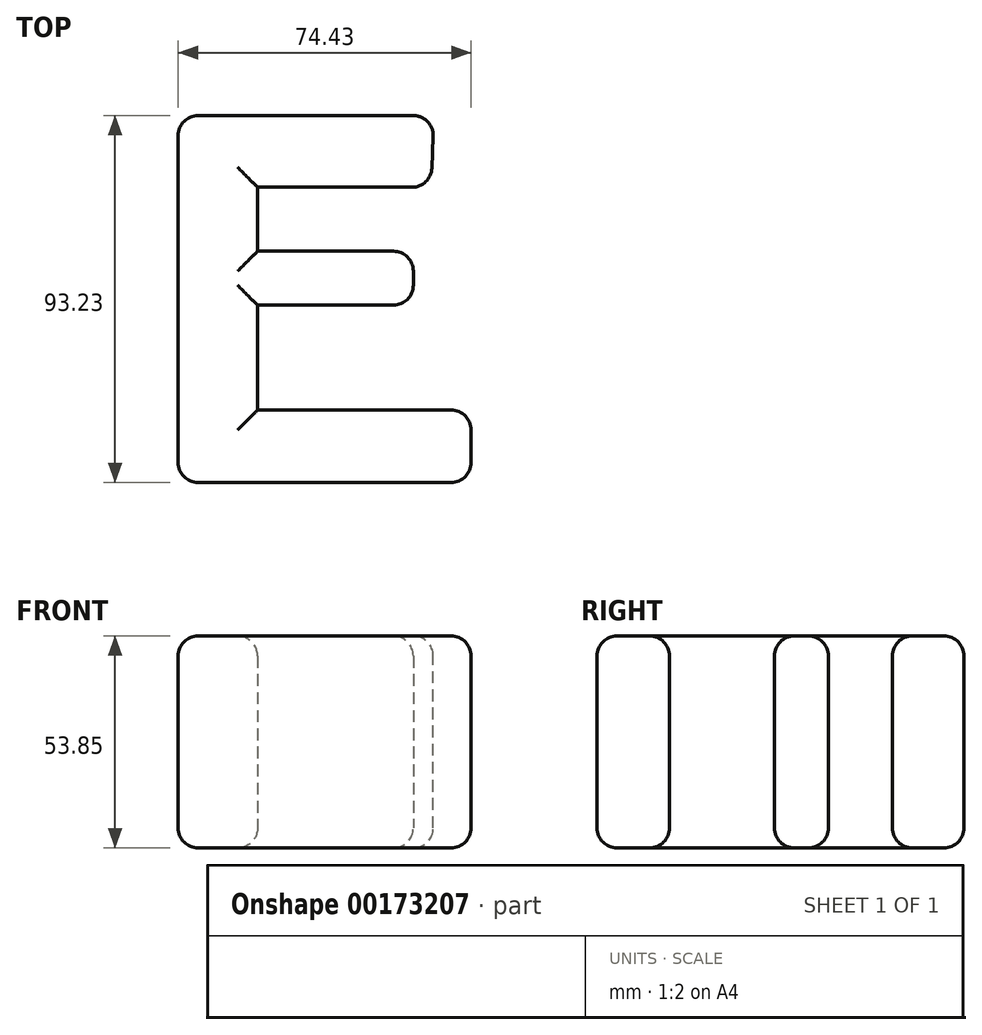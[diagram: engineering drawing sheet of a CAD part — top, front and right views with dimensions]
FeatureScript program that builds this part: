
annotation { "Feature Type Name" : "Feature", "Feature Type Description" : "" }
export const myFeature = defineFeature(function(context is Context, id is Id, definition is map)
    precondition{}
    {
        {
            var Q0;
            Q0=qCreatedBy(makeId("Top.planeOp"),FACE);
            var sketch = newSketch(context, id + "F0", { "sketchPlane" : qUnion([Q0])});
            skLineSegment(sketch, "E0", {"start": v(28, 52) * mm, "end": v(-37.02, 52) * mm});
            skLineSegment(sketch, "E1", {"start": v(-37.02, 52) * mm, "end": v(-37.02, -41.23) * mm});
            skLineSegment(sketch, "E2", {"start": v(-37.02, -41.23) * mm, "end": v(37.4, -41.23) * mm});
            skLineSegment(sketch, "E3", {"start": v(37.4, -41.23) * mm, "end": v(37.4, -22.82) * mm});
            skLineSegment(sketch, "E4", {"start": v(37.4, -22.82) * mm, "end": v(-16.84, -22.82) * mm});
            skLineSegment(sketch, "E5", {"start": v(-16.84, -22.82) * mm, "end": v(-16.84, -6.56) * mm});
            skLineSegment(sketch, "E6", {"start": v(-16.84, -6.56) * mm, "end": v(-16.84, 3.82) * mm});
            skLineSegment(sketch, "E7", {"start": v(-16.84, 3.82) * mm, "end": v(22.72, 3.82) * mm});
            skLineSegment(sketch, "E8", {"start": v(22.72, 3.82) * mm, "end": v(22.72, 17.53) * mm});
            skLineSegment(sketch, "E9", {"start": v(22.72, 17.53) * mm, "end": v(-16.84, 17.53) * mm});
            skLineSegment(sketch, "E10", {"start": v(-16.84, 17.53) * mm, "end": v(-16.84, 33.79) * mm});
            skLineSegment(sketch, "E11", {"start": v(-16.84, 33.79) * mm, "end": v(27.22, 33.79) * mm});
            skLineSegment(sketch, "E12", {"start": v(28, 52) * mm, "end": v(27.22, 33.79) * mm});
            skSolve(sketch);
        }
        {
            var Q0;
            Q0=makeQuery(id+"F0.imprint","IMPRINT",FACE,{"disambiguationData":[TD([[makeQuery(id+"F0.imprint","IMPRINT",EDGE,{"derivedFrom":sQuery(id+"F0.wireOp",EDGE,"E0")}),1.0]])]});
            extrude(context, id + "F1", {"entities" : qUnion([Q0]), "depth" : 53.85 * mm});
        }
        {
            var Q0;
            Q0=makeQuery(id+"F1.opExtrude","SWEPT_FACE",FACE,{"disambiguationData":[OSD([sQuery(id+"F0.wireOp",EDGE,"E12")])]});
            var Q1;
            Q1=makeQuery(id+"F1.opExtrude","SWEPT_FACE",FACE,{"disambiguationData":[OSD([sQuery(id+"F0.wireOp",EDGE,"E8")])]});
            var Q2;
            Q2=makeQuery(id+"F1.opExtrude","SWEPT_FACE",FACE,{"disambiguationData":[OSD([sQuery(id+"F0.wireOp",EDGE,"E3")])]});
            fillet(context, id + "F2", {"entities" : qUnion([Q0, Q1, Q2]), "radius" : 5.08 * mm, "tangentPropagation" : true, "allowEdgeOverflow" : false});
        }
        {
            var Q0;
            Q0=makeQuery(id+"F1.opExtrude","CAP_EDGE",EDGE,{"disambiguationData":[OSD([sQuery(id+"F0.wireOp",EDGE,"E2")])],"isStart":false});
            var Q1;
            Q1=makeQuery(id+"F1.opExtrude","CAP_EDGE",EDGE,{"disambiguationData":[OSD([sQuery(id+"F0.wireOp",EDGE,"E1")])],"isStart":false});
            var Q2;
            Q2=makeQuery(id+"F1.opExtrude","CAP_EDGE",EDGE,{"disambiguationData":[OSD([sQuery(id+"F0.wireOp",EDGE,"E0")])],"isStart":false});
            var Q3;
            Q3=makeQuery(id+"F1.opExtrude","CAP_EDGE",EDGE,{"disambiguationData":[OSD([sQuery(id+"F0.wireOp",EDGE,"E10")])],"isStart":false});
            var Q4;
            Q4=makeQuery(id+"F1.opExtrude","CAP_EDGE",EDGE,{"disambiguationData":[OSD([sQuery(id+"F0.wireOp",EDGE,"E11")])],"isStart":false});
            var Q5;
            Q5=makeQuery(id+"F1.opExtrude","CAP_EDGE",EDGE,{"disambiguationData":[OSD([sQuery(id+"F0.wireOp",EDGE,"E9")])],"isStart":false});
            var Q6;
            Q6=makeQuery(id+"F1.opExtrude","CAP_EDGE",EDGE,{"disambiguationData":[OSD([sQuery(id+"F0.wireOp",EDGE,"E7")])],"isStart":false});
            var Q7;
            Q7=makeQuery(id+"F1.opExtrude","CAP_EDGE",EDGE,{"disambiguationData":[OSD([sQuery(id+"F0.wireOp",EDGE,"E5"),sQuery(id+"F0.wireOp",EDGE,"E6")])],"isStart":false});
            var Q8;
            Q8=makeQuery(id+"F1.opExtrude","CAP_EDGE",EDGE,{"disambiguationData":[OSD([sQuery(id+"F0.wireOp",EDGE,"E4")])],"isStart":false});
            fillet(context, id + "F3", {"entities" : qUnion([Q0, Q1, Q2, Q3, Q4, Q5, Q6, Q7, Q8]), "radius" : 5.08 * mm, "tangentPropagation" : true, "allowEdgeOverflow" : false});
        }
        {
            var Q0;
            Q0=makeQuery(id+"F1.opExtrude","CAP_EDGE",EDGE,{"disambiguationData":[OSD([sQuery(id+"F0.wireOp",EDGE,"E4")])],"isStart":true});
            var Q1;
            Q1=makeQuery(id+"F1.opExtrude","CAP_EDGE",EDGE,{"disambiguationData":[OSD([sQuery(id+"F0.wireOp",EDGE,"E2")])],"isStart":true});
            var Q2;
            Q2=makeQuery(id+"F1.opExtrude","CAP_EDGE",EDGE,{"disambiguationData":[OSD([sQuery(id+"F0.wireOp",EDGE,"E5"),sQuery(id+"F0.wireOp",EDGE,"E6")])],"isStart":true});
            var Q3;
            Q3=makeQuery(id+"F1.opExtrude","CAP_EDGE",EDGE,{"disambiguationData":[OSD([sQuery(id+"F0.wireOp",EDGE,"E7")])],"isStart":true});
            var Q4;
            Q4=makeQuery(id+"F1.opExtrude","CAP_EDGE",EDGE,{"disambiguationData":[OSD([sQuery(id+"F0.wireOp",EDGE,"E9")])],"isStart":true});
            var Q5;
            Q5=makeQuery(id+"F1.opExtrude","CAP_EDGE",EDGE,{"disambiguationData":[OSD([sQuery(id+"F0.wireOp",EDGE,"E10")])],"isStart":true});
            var Q6;
            Q6=makeQuery(id+"F1.opExtrude","CAP_EDGE",EDGE,{"disambiguationData":[OSD([sQuery(id+"F0.wireOp",EDGE,"E11")])],"isStart":true});
            var Q7;
            Q7=makeQuery(id+"F1.opExtrude","CAP_EDGE",EDGE,{"disambiguationData":[OSD([sQuery(id+"F0.wireOp",EDGE,"E0")])],"isStart":true});
            var Q8;
            Q8=makeQuery(id+"F1.opExtrude","CAP_EDGE",EDGE,{"disambiguationData":[OSD([sQuery(id+"F0.wireOp",EDGE,"E1")])],"isStart":true});
            fillet(context, id + "F4", {"entities" : qUnion([Q0, Q1, Q2, Q3, Q4, Q5, Q6, Q7, Q8]), "radius" : 5.08 * mm, "tangentPropagation" : true, "allowEdgeOverflow" : false});
        }
        {
            var Q0;
            Q0=makeQuery(id+"F1.opExtrude","SWEPT_EDGE",EDGE,{"disambiguationData":[OSD([sQuery(id+"F0.wireOp",EDGE,"E0"),sQuery(id+"F0.wireOp",EDGE,"E1")])]});
            var Q1;
            Q1=makeQuery(id+"F1.opExtrude","SWEPT_FACE",FACE,{"disambiguationData":[OSD([sQuery(id+"F0.wireOp",EDGE,"E2")])]});
            fillet(context, id + "F5", {"entities" : qUnion([Q0, Q1]), "radius" : 5.08 * mm, "tangentPropagation" : true, "allowEdgeOverflow" : false});
        }
    });
